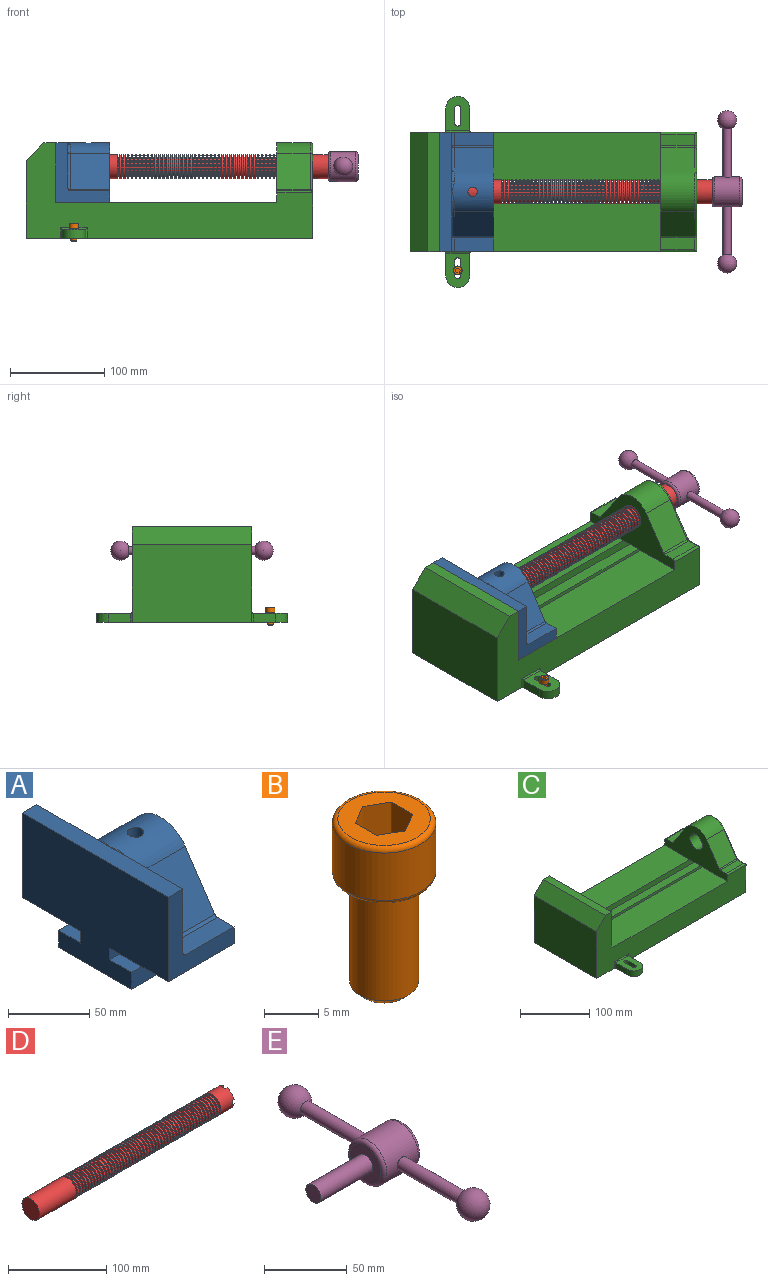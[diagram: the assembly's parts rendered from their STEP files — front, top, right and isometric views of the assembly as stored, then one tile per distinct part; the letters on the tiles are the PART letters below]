
ASSEMBLY  parts=5 mates=5
PART A: 36 faces, bbox 57.2x127x89 mm
  f0: plane 57.15x50.8mm, normal (0,0,-1), area 2903.2mm2, adj f6,f9,f10,f23
  f1: cylinder r=12.7mm len=44.45mm, axis (1,0,0), area 3464.3mm2, adj f6,f15,f16
  f2: plane 41.91x14.52mm, normal (0,0,1), area 608.5mm2, adj f6,f11,f24,f25
  f3: plane 51.86x48.26mm, normal (1,0,0), area 1495.7mm2, adj f8,f10,f31,f33,f35
  f4: plane 51.86x48.26mm, normal (1,0,0), area 1495.7mm2, adj f8,f11,f24,f28,f29
  f5: plane 57.15x50.8mm, normal (0,0,-1), area 2903.2mm2, adj f6,f9,f11,f22
  f6: plane 127x85.09mm, normal (1,0,0), area 5190.6mm2, adj f0,f1,f2,f5,f7,f10,f11,f12
  f7: plane 41.91x14.52mm, normal (0,0,1), area 608.5mm2, adj f6,f10,f30,f31
  f8: plane 127x12.7mm, normal (0,0,1), area 1612.9mm2, adj f3,f4,f9,f10,f11,f26,f34
  f9: plane 127x85.09mm, normal (-1,0,0), area 9096.8mm2, adj f0,f5,f8,f10,f11,f17,f18,f19
  f10: plane 63.5x57.15mm, normal (0,-1,0), area 1372.3mm2, adj f0,f3,f6,f7,f8,f9,f31
  f11: plane 63.5x57.15mm, normal (0,1,0), area 1372.3mm2, adj f2,f4,f5,f6,f8,f9,f24
  f12: plane 41.91x38.43mm, normal (0,-0.83,0.56), area 1939.2mm2, adj f6,f13,f30,f33
  f13: cylinder r=25.4mm len=44.45mm, axis (1,0,0), area 2026.5mm2, adj f6,f12,f14,f16,f26,f28,f34,f35
  f14: plane 41.91x38.43mm, normal (0,0.83,0.56), area 1939.2mm2, adj f6,f13,f25,f29
  f15: plane 25.4x25.4mm, normal (1,0,0), area 506.7mm2, adj f1
  f16: cylinder r=5.08mm len=13.76mm, axis (0,0,1), area 414mm2, adj f1,f13
  f17: plane 57.15x19.05mm, normal (0,0,1), area 1088.7mm2, adj f6,f9,f18,f23
  f18: plane 57.15x12.7mm, normal (0,-1,0), area 725.8mm2, adj f6,f9,f17,f19
  f19: plane 63.5x57.15mm, normal (0,0,-1), area 3629mm2, adj f6,f9,f18,f20
  f20: plane 57.15x12.7mm, normal (0,1,0), area 725.8mm2, adj f6,f9,f19,f21
  f21: plane 57.15x19.05mm, normal (0,0,1), area 1088.7mm2, adj f6,f9,f20,f22
  f22: plane 57.15x8.89mm, normal (0,1,0), area 508.1mm2, adj f5,f6,f9,f21
  f23: plane 57.15x8.89mm, normal (0,-1,0), area 508.1mm2, adj f0,f6,f9,f17
  f24: cylinder r=2.54mm len=14.52mm, axis (0,-1,0), area 57.9mm2, adj f2,f4,f11,f27
  f25: cylinder r=2.54mm len=41.91mm, axis (1,0,0), area 104.3mm2, adj f2,f6,f14,f27
  f26: bspline ~12.24x2.8mm, area 20.9mm2, adj f8,f13,f28
  f27: sphere r=2.54mm, area 6.3mm2, adj f24,f25,f29
  f28: torus R=27.94mm, axis (1,0,0), area 57.8mm2, adj f4,f13,f26,f29
  f29: cylinder r=2.54mm len=39.84mm, axis (0,-0.56,0.83), area 184.6mm2, adj f4,f14,f27,f28
  f30: cylinder r=2.54mm len=41.91mm, axis (1,0,0), area 104.3mm2, adj f6,f7,f12,f32
  f31: cylinder r=2.54mm len=14.52mm, axis (0,-1,0), area 57.9mm2, adj f3,f7,f10,f32
  f32: sphere r=2.54mm, area 6.3mm2, adj f30,f31,f33
  f33: cylinder r=2.54mm len=39.84mm, axis (0,-0.56,-0.83), area 184.6mm2, adj f3,f12,f32,f35
  f34: bspline ~12.24x2.8mm, area 20.9mm2, adj f8,f13,f35
  f35: torus R=27.94mm, axis (1,0,0), area 57.8mm2, adj f3,f13,f33,f34
PART B: 15 faces, bbox 10.3x10.3x19.1 mm
  f0: plane 8.51x8.51mm, normal (0,0,1), area 37.2mm2, adj f5,f6,f7,f8,f9,f10,f14
  f1: cylinder r=3.17mm len=11.94mm, axis (0,0,1), area 238.2mm2, adj f4,f12
  f2: plane 4.83x4.83mm, normal (0,0,-1), area 18.3mm2, adj f12
  f3: cylinder r=4.76mm len=9.53mm, axis (0,0,-1), area 159.6mm2, adj f13,f14
  f4: plane 8.51x8.51mm, normal (0,0,-1), area 25.2mm2, adj f1,f13
  f5: plane 4.83x2.38mm, normal (-0.5,-0.87,0), area 13.3mm2, adj f0,f6,f10,f11
  f6: plane 4.83x2.38mm, normal (0.5,-0.87,0), area 13.3mm2, adj f0,f5,f7,f11
  f7: plane 4.83x2.75mm, normal (1,0,0), area 13.3mm2, adj f0,f6,f8,f11
  f8: plane 4.83x2.38mm, normal (0.5,0.87,0), area 13.3mm2, adj f0,f7,f9,f11
  f9: plane 4.83x2.38mm, normal (-0.5,0.87,0), area 13.3mm2, adj f0,f8,f10,f11
  f10: plane 4.83x2.75mm, normal (-1,0,0), area 13.3mm2, adj f0,f5,f9,f11
  f11: plane 5.5x4.76mm, normal (0,0,1), area 19.6mm2, adj f5,f6,f7,f8,f9,f10
  f12: cone r=3.17mm half-angle=45deg, axis (0,0,1), area 18.9mm2, adj f1,f2
  f13: torus R=4.25mm, axis (0,0,1), area 23mm2, adj f3,f4
  f14: torus R=4.25mm, axis (0,0,1), area 23mm2, adj f0,f3
PART C: 61 faces, bbox 304.8x203.2x103.7 mm
  f0: plane 304.8x101.6mm, normal (0,1,0), area 13520.3mm2, adj f3,f4,f5,f6,f7,f8,f9,f16
  f1: plane 304.8x101.6mm, normal (0,-1,0), area 13520.3mm2, adj f2,f3,f5,f6,f7,f8,f9,f16
  f2: plane 234.95x50.8mm, normal (0,0,1), area 11935.5mm2, adj f1,f5,f16,f26
  f3: plane 127x99.06mm, normal (1,0,0), area 7097.5mm2, adj f0,f1,f9,f14,f17,f18,f19,f20
  f4: plane 234.95x50.8mm, normal (0,0,1), area 11935.5mm2, adj f0,f5,f16,f27
  f5: plane 127x101.6mm, normal (1,0,0), area 9516.1mm2, adj f0,f1,f2,f4,f6,f9,f18,f19
  f6: plane 127x12.7mm, normal (0,0,1), area 1612.9mm2, adj f0,f1,f5,f7
  f7: plane 127x19.05mm, normal (-0.71,0,0.71), area 3421.5mm2, adj f0,f1,f6,f8
  f8: plane 127x82.55mm, normal (-1,0,0), area 10483.8mm2, adj f0,f1,f7,f9
  f9: plane 304.8x203.2mm, normal (0,0,-1), area 33298.3mm2, adj f0,f1,f3,f5,f8,f21,f22,f39
  f10: plane 35.56x11.98mm, normal (0,0,1), area 426mm2, adj f16,f28,f29,f30
  f11: plane 38.43x35.56mm, normal (0,0.83,0.56), area 1645.4mm2, adj f12,f16,f29,f32
  f12: cylinder r=25.4mm len=42.19mm, axis (1,0,0), area 1770.2mm2, adj f11,f13,f16,f33
  f13: plane 38.43x35.56mm, normal (0,-0.83,0.56), area 1645.4mm2, adj f12,f16,f34,f35
  f14: cylinder r=12.7mm len=38.1mm, axis (1,0,0), area 3040.2mm2, adj f3,f16
  f15: plane 35.56x11.98mm, normal (0,0,1), area 426mm2, adj f16,f34,f36,f38
  f16: plane 127x63.5mm, normal (-1,0,0), area 4155.5mm2, adj f0,f1,f2,f4,f10,f11,f12,f13
  f17: plane 38.1x25.4mm, normal (0,0,-1), area 967.7mm2, adj f3,f16,f26,f27
  f18: plane 273.05x19.05mm, normal (0,0,-1), area 5201.6mm2, adj f3,f5,f19,f26
  f19: plane 273.05x12.7mm, normal (0,1,0), area 3467.7mm2, adj f3,f5,f18,f20
  f20: plane 273.05x19.05mm, normal (0,0,1), area 5201.6mm2, adj f3,f5,f19,f21
  f21: plane 273.05x16.51mm, normal (0,1,0), area 4508.1mm2, adj f3,f5,f9,f20
  f22: plane 273.05x16.51mm, normal (0,-1,0), area 4508.1mm2, adj f3,f5,f9,f23
  f23: plane 273.05x19.05mm, normal (0,0,1), area 5201.6mm2, adj f3,f5,f22,f24
  f24: plane 273.05x12.7mm, normal (0,-1,0), area 3467.7mm2, adj f3,f5,f23,f25
  f25: plane 273.05x19.05mm, normal (0,0,-1), area 5201.6mm2, adj f3,f5,f24,f27
  f26: plane 273.05x8.89mm, normal (0,1,0), area 2427.4mm2, adj f2,f3,f5,f17,f18
  f27: plane 273.05x8.89mm, normal (0,-1,0), area 2427.4mm2, adj f3,f4,f5,f17,f25
  f28: cylinder r=2.54mm len=38.1mm, axis (1,0,0), area 148.3mm2, adj f0,f10,f16,f30
  f29: cylinder r=2.54mm len=35.56mm, axis (-1,0,0), area 88.5mm2, adj f10,f11,f16,f31
  f30: cylinder r=2.54mm len=14.52mm, axis (0,1,0), area 54.3mm2, adj f3,f10,f28,f31
  f31: torus R=5.08mm, axis (-1,0,0), area 13.5mm2, adj f3,f29,f30,f32
  f32: cylinder r=2.54mm len=39.84mm, axis (0,0.56,-0.83), area 184.6mm2, adj f3,f11,f31,f33
  f33: torus R=22.86mm, axis (-1,0,0), area 191.4mm2, adj f3,f12,f32,f35
  f34: cylinder r=2.54mm len=35.56mm, axis (-1,0,0), area 88.5mm2, adj f13,f15,f16,f37
  f35: cylinder r=2.54mm len=39.84mm, axis (0,0.56,0.83), area 184.6mm2, adj f3,f13,f33,f37
  f36: cylinder r=2.54mm len=38.1mm, axis (-1,0,0), area 148.3mm2, adj f1,f15,f16,f38
  f37: torus R=5.08mm, axis (-1,0,0), area 13.5mm2, adj f3,f34,f35,f38
  f38: cylinder r=2.54mm len=14.52mm, axis (0,1,0), area 54.3mm2, adj f3,f15,f36,f37
  f39: plane 23.88x9.53mm, normal (-1,0,0), area 227.4mm2, adj f9,f45,f46,f60
  f40: plane 23.88x9.53mm, normal (1,0,0), area 227.4mm2, adj f9,f45,f46,f58
  f41: cylinder r=3.3mm len=9.53mm, axis (0,0,-1), area 98.8mm2, adj f9,f42,f44,f46
  f42: plane 15.62x9.53mm, normal (-1,0,0), area 148.8mm2, adj f9,f41,f43,f46
  f43: cylinder r=3.3mm len=9.53mm, axis (0,0,-1), area 98.8mm2, adj f9,f42,f44,f46
  f44: plane 15.62x9.53mm, normal (1,0,0), area 148.8mm2, adj f9,f41,f43,f46
  f45: cylinder r=12.7mm len=25.4mm, axis (0,0,-1), area 380mm2, adj f9,f39,f40,f46
  f46: plane 36.58x25.4mm, normal (0,0,1), area 722.4mm2, adj f39,f40,f41,f42,f43,f44,f45,f59
  f47: plane 23.88x9.53mm, normal (-1,0,0), area 227.4mm2, adj f9,f53,f54,f56
  f48: plane 23.88x9.53mm, normal (1,0,0), area 227.4mm2, adj f9,f53,f54,f55
  f49: cylinder r=3.3mm len=9.53mm, axis (0,0,-1), area 98.8mm2, adj f9,f50,f52,f54
  f50: plane 15.62x9.53mm, normal (-1,0,0), area 148.8mm2, adj f9,f49,f51,f54
  f51: cylinder r=3.3mm len=9.53mm, axis (0,0,-1), area 98.8mm2, adj f9,f50,f52,f54
  f52: plane 15.62x9.53mm, normal (1,0,0), area 148.8mm2, adj f9,f49,f51,f54
  f53: cylinder r=12.7mm len=25.4mm, axis (0,0,-1), area 380mm2, adj f9,f47,f48,f54
  f54: plane 36.58x25.4mm, normal (0,0,1), area 722.4mm2, adj f47,f48,f49,f50,f51,f52,f53,f57
  f55: cylinder r=1.52mm len=11.05mm, axis (0,0,-1), area 24.1mm2, adj f0,f9,f48,f57
  f56: cylinder r=1.52mm len=11.05mm, axis (0,0,1), area 24.1mm2, adj f0,f9,f47,f57
  f57: cylinder r=1.52mm len=28.45mm, axis (1,0,0), area 63.5mm2, adj f0,f54,f55,f56
  f58: cylinder r=1.52mm len=11.05mm, axis (0,0,1), area 24.1mm2, adj f1,f9,f40,f59
  f59: cylinder r=1.52mm len=28.45mm, axis (-1,0,0), area 63.5mm2, adj f1,f46,f58,f60
  f60: cylinder r=1.52mm len=11.05mm, axis (0,0,-1), area 24.1mm2, adj f1,f9,f39,f59
PART D: 220 faces, bbox 279.4x25.4x25.4 mm
  f0: cylinder r=12.7mm len=25.4mm, axis (-1,0,0), area 1468.2mm2, adj f1,f2,f3,f5,f7,f208,f209,f210
  f1: plane 9.9x9.9mm, normal (1,0,0), area 62.3mm2, adj f0,f4,f213,f216
  f2: plane 9.9x9.9mm, normal (1,0,0), area 62.3mm2, adj f0,f4,f210,f218
  f3: plane 9.9x9.9mm, normal (1,0,0), area 62.3mm2, adj f0,f4,f209,f212
  f4: cylinder r=6.35mm len=25.4mm, axis (1,0,0), area 960.3mm2, adj f1,f2,f3,f5,f6,f208,f209,f210
  f5: plane 9.9x9.9mm, normal (1,0,0), area 62.3mm2, adj f0,f4,f215,f217
  f6: plane 12.7x12.7mm, normal (1,0,0), area 126.7mm2, adj f4
  f7: cone r=12.7mm half-angle=76deg, axis (1,0,0), area 188mm2, adj f0,f9
  f8: cone r=10.16mm half-angle=76deg, axis (-1,0,0), area 188mm2, adj f9,f10
  f9: cylinder r=10.16mm len=20.32mm, axis (1,0,0), area 81.1mm2, adj f7,f8
  f10: cylinder r=12.7mm len=25.4mm, axis (-1,0,0), area 131.7mm2, adj f8,f11
  f11: cone r=12.7mm half-angle=76deg, axis (1,0,0), area 188mm2, adj f10,f13
  f12: cone r=10.16mm half-angle=76deg, axis (-1,0,0), area 188mm2, adj f13,f14
  f13: cylinder r=10.16mm len=20.32mm, axis (1,0,0), area 81.1mm2, adj f11,f12
  f14: cylinder r=12.7mm len=25.4mm, axis (-1,0,0), area 131.7mm2, adj f12,f15
  f15: cone r=12.7mm half-angle=76deg, axis (1,0,0), area 188mm2, adj f14,f17
  f16: cone r=10.16mm half-angle=76deg, axis (-1,0,0), area 188mm2, adj f17,f18
  f17: cylinder r=10.16mm len=20.32mm, axis (1,0,0), area 81.1mm2, adj f15,f16
  f18: cylinder r=12.7mm len=25.4mm, axis (-1,0,0), area 131.7mm2, adj f16,f19
  f19: cone r=12.7mm half-angle=76deg, axis (1,0,0), area 188mm2, adj f18,f21
  f20: cone r=10.16mm half-angle=76deg, axis (-1,0,0), area 188mm2, adj f21,f22
  f21: cylinder r=10.16mm len=20.32mm, axis (1,0,0), area 81.1mm2, adj f19,f20
  f22: cylinder r=12.7mm len=25.4mm, axis (-1,0,0), area 131.7mm2, adj f20,f23
  f23: cone r=12.7mm half-angle=76deg, axis (1,0,0), area 188mm2, adj f22,f25
  f24: cone r=10.16mm half-angle=76deg, axis (-1,0,0), area 188mm2, adj f25,f26
  f25: cylinder r=10.16mm len=20.32mm, axis (1,0,0), area 81.1mm2, adj f23,f24
  f26: cylinder r=12.7mm len=25.4mm, axis (-1,0,0), area 131.7mm2, adj f24,f27
  f27: cone r=12.7mm half-angle=76deg, axis (1,0,0), area 188mm2, adj f26,f29
  f28: cone r=10.16mm half-angle=76deg, axis (-1,0,0), area 188mm2, adj f29,f30
  f29: cylinder r=10.16mm len=20.32mm, axis (1,0,0), area 81.1mm2, adj f27,f28
  f30: cylinder r=12.7mm len=25.4mm, axis (-1,0,0), area 131.7mm2, adj f28,f31
  f31: cone r=12.7mm half-angle=76deg, axis (1,0,0), area 188mm2, adj f30,f33
  f32: cone r=10.16mm half-angle=76deg, axis (-1,0,0), area 188mm2, adj f33,f34
  f33: cylinder r=10.16mm len=20.32mm, axis (1,0,0), area 81.1mm2, adj f31,f32
  f34: cylinder r=12.7mm len=25.4mm, axis (-1,0,0), area 131.7mm2, adj f32,f35
  f35: cone r=12.7mm half-angle=76deg, axis (1,0,0), area 188mm2, adj f34,f37
  f36: cone r=10.16mm half-angle=76deg, axis (-1,0,0), area 188mm2, adj f37,f38
  f37: cylinder r=10.16mm len=20.32mm, axis (1,0,0), area 81.1mm2, adj f35,f36
  f38: cylinder r=12.7mm len=25.4mm, axis (-1,0,0), area 131.7mm2, adj f36,f39
  f39: cone r=12.7mm half-angle=76deg, axis (1,0,0), area 188mm2, adj f38,f41
  f40: cone r=10.16mm half-angle=76deg, axis (-1,0,0), area 188mm2, adj f41,f42
  f41: cylinder r=10.16mm len=20.32mm, axis (1,0,0), area 81.1mm2, adj f39,f40
  f42: cylinder r=12.7mm len=25.4mm, axis (-1,0,0), area 131.7mm2, adj f40,f43
  f43: cone r=12.7mm half-angle=76deg, axis (1,0,0), area 188mm2, adj f42,f45
  f44: cone r=10.16mm half-angle=76deg, axis (-1,0,0), area 188mm2, adj f45,f46
  f45: cylinder r=10.16mm len=20.32mm, axis (1,0,0), area 81.1mm2, adj f43,f44
  f46: cylinder r=12.7mm len=25.4mm, axis (-1,0,0), area 131.7mm2, adj f44,f47
  f47: cone r=12.7mm half-angle=76deg, axis (1,0,0), area 188mm2, adj f46,f49
  f48: cone r=10.16mm half-angle=76deg, axis (-1,0,0), area 188mm2, adj f49,f50
  f49: cylinder r=10.16mm len=20.32mm, axis (1,0,0), area 81.1mm2, adj f47,f48
  f50: cylinder r=12.7mm len=25.4mm, axis (-1,0,0), area 131.7mm2, adj f48,f51
  f51: cone r=12.7mm half-angle=76deg, axis (1,0,0), area 188mm2, adj f50,f53
  f52: cone r=10.16mm half-angle=76deg, axis (-1,0,0), area 188mm2, adj f53,f54
  f53: cylinder r=10.16mm len=20.32mm, axis (1,0,0), area 81.1mm2, adj f51,f52
  f54: cylinder r=12.7mm len=25.4mm, axis (-1,0,0), area 131.7mm2, adj f52,f55
  f55: cone r=12.7mm half-angle=76deg, axis (1,0,0), area 188mm2, adj f54,f57
  f56: cone r=10.16mm half-angle=76deg, axis (-1,0,0), area 188mm2, adj f57,f58
  f57: cylinder r=10.16mm len=20.32mm, axis (1,0,0), area 81.1mm2, adj f55,f56
  f58: cylinder r=12.7mm len=25.4mm, axis (-1,0,0), area 131.7mm2, adj f56,f59
  f59: cone r=12.7mm half-angle=76deg, axis (1,0,0), area 188mm2, adj f58,f61
  f60: cone r=10.16mm half-angle=76deg, axis (-1,0,0), area 188mm2, adj f61,f62
  f61: cylinder r=10.16mm len=20.32mm, axis (1,0,0), area 81.1mm2, adj f59,f60
  f62: cylinder r=12.7mm len=25.4mm, axis (-1,0,0), area 131.7mm2, adj f60,f63
  f63: cone r=12.7mm half-angle=76deg, axis (1,0,0), area 188mm2, adj f62,f65
  f64: cone r=10.16mm half-angle=76deg, axis (-1,0,0), area 188mm2, adj f65,f66
  f65: cylinder r=10.16mm len=20.32mm, axis (1,0,0), area 81.1mm2, adj f63,f64
  f66: cylinder r=12.7mm len=25.4mm, axis (-1,0,0), area 131.7mm2, adj f64,f67
  f67: cone r=12.7mm half-angle=76deg, axis (1,0,0), area 188mm2, adj f66,f69
  f68: cone r=10.16mm half-angle=76deg, axis (-1,0,0), area 188mm2, adj f69,f70
  f69: cylinder r=10.16mm len=20.32mm, axis (1,0,0), area 81.1mm2, adj f67,f68
  f70: cylinder r=12.7mm len=25.4mm, axis (-1,0,0), area 131.7mm2, adj f68,f71
  f71: cone r=12.7mm half-angle=76deg, axis (1,0,0), area 188mm2, adj f70,f73
  f72: cone r=10.16mm half-angle=76deg, axis (-1,0,0), area 188mm2, adj f73,f74
  f73: cylinder r=10.16mm len=20.32mm, axis (1,0,0), area 81.1mm2, adj f71,f72
  f74: cylinder r=12.7mm len=25.4mm, axis (-1,0,0), area 131.7mm2, adj f72,f75
  f75: cone r=12.7mm half-angle=76deg, axis (1,0,0), area 188mm2, adj f74,f77
  f76: cone r=10.16mm half-angle=76deg, axis (-1,0,0), area 188mm2, adj f77,f78
  f77: cylinder r=10.16mm len=20.32mm, axis (1,0,0), area 81.1mm2, adj f75,f76
  f78: cylinder r=12.7mm len=25.4mm, axis (-1,0,0), area 131.7mm2, adj f76,f79
  f79: cone r=12.7mm half-angle=76deg, axis (1,0,0), area 188mm2, adj f78,f81
  f80: cone r=10.16mm half-angle=76deg, axis (-1,0,0), area 188mm2, adj f81,f82
  f81: cylinder r=10.16mm len=20.32mm, axis (1,0,0), area 81.1mm2, adj f79,f80
  f82: cylinder r=12.7mm len=25.4mm, axis (-1,0,0), area 131.7mm2, adj f80,f83
  f83: cone r=12.7mm half-angle=76deg, axis (1,0,0), area 188mm2, adj f82,f85
  f84: cone r=10.16mm half-angle=76deg, axis (-1,0,0), area 188mm2, adj f85,f86
  f85: cylinder r=10.16mm len=20.32mm, axis (1,0,0), area 81.1mm2, adj f83,f84
  f86: cylinder r=12.7mm len=25.4mm, axis (-1,0,0), area 131.7mm2, adj f84,f87
  f87: cone r=12.7mm half-angle=76deg, axis (1,0,0), area 188mm2, adj f86,f89
  f88: cone r=10.16mm half-angle=76deg, axis (-1,0,0), area 188mm2, adj f89,f90
  f89: cylinder r=10.16mm len=20.32mm, axis (1,0,0), area 81.1mm2, adj f87,f88
  f90: cylinder r=12.7mm len=25.4mm, axis (-1,0,0), area 131.7mm2, adj f88,f91
  f91: cone r=12.7mm half-angle=76deg, axis (1,0,0), area 188mm2, adj f90,f93
  f92: cone r=10.16mm half-angle=76deg, axis (-1,0,0), area 188mm2, adj f93,f94
  f93: cylinder r=10.16mm len=20.32mm, axis (1,0,0), area 81.1mm2, adj f91,f92
  f94: cylinder r=12.7mm len=25.4mm, axis (-1,0,0), area 131.7mm2, adj f92,f95
  f95: cone r=12.7mm half-angle=76deg, axis (1,0,0), area 188mm2, adj f94,f97
  f96: cone r=10.16mm half-angle=76deg, axis (-1,0,0), area 188mm2, adj f97,f98
  f97: cylinder r=10.16mm len=20.32mm, axis (1,0,0), area 81.1mm2, adj f95,f96
  f98: cylinder r=12.7mm len=25.4mm, axis (-1,0,0), area 131.7mm2, adj f96,f99
  f99: cone r=12.7mm half-angle=76deg, axis (1,0,0), area 188mm2, adj f98,f101
  f100: cone r=10.16mm half-angle=76deg, axis (-1,0,0), area 188mm2, adj f101,f102
  f101: cylinder r=10.16mm len=20.32mm, axis (1,0,0), area 81.1mm2, adj f99,f100
  f102: cylinder r=12.7mm len=25.4mm, axis (-1,0,0), area 131.7mm2, adj f100,f103
  f103: cone r=12.7mm half-angle=76deg, axis (1,0,0), area 188mm2, adj f102,f105
  f104: cone r=10.16mm half-angle=76deg, axis (-1,0,0), area 188mm2, adj f105,f106
  f105: cylinder r=10.16mm len=20.32mm, axis (1,0,0), area 81.1mm2, adj f103,f104
  f106: cylinder r=12.7mm len=25.4mm, axis (-1,0,0), area 131.7mm2, adj f104,f107
  f107: cone r=12.7mm half-angle=76deg, axis (1,0,0), area 188mm2, adj f106,f109
  f108: cone r=10.16mm half-angle=76deg, axis (-1,0,0), area 188mm2, adj f109,f110
  f109: cylinder r=10.16mm len=20.32mm, axis (1,0,0), area 81.1mm2, adj f107,f108
  f110: cylinder r=12.7mm len=25.4mm, axis (-1,0,0), area 131.7mm2, adj f108,f111
  f111: cone r=12.7mm half-angle=76deg, axis (1,0,0), area 188mm2, adj f110,f113
  f112: cone r=10.16mm half-angle=76deg, axis (-1,0,0), area 188mm2, adj f113,f114
  f113: cylinder r=10.16mm len=20.32mm, axis (1,0,0), area 81.1mm2, adj f111,f112
  f114: cylinder r=12.7mm len=25.4mm, axis (-1,0,0), area 131.7mm2, adj f112,f115
  f115: cone r=12.7mm half-angle=76deg, axis (1,0,0), area 188mm2, adj f114,f117
  f116: cone r=10.16mm half-angle=76deg, axis (-1,0,0), area 188mm2, adj f117,f118
  f117: cylinder r=10.16mm len=20.32mm, axis (1,0,0), area 81.1mm2, adj f115,f116
  f118: cylinder r=12.7mm len=25.4mm, axis (-1,0,0), area 131.7mm2, adj f116,f119
  f119: cone r=12.7mm half-angle=76deg, axis (1,0,0), area 188mm2, adj f118,f121
  f120: cone r=10.16mm half-angle=76deg, axis (-1,0,0), area 188mm2, adj f121,f122
  f121: cylinder r=10.16mm len=20.32mm, axis (1,0,0), area 81.1mm2, adj f119,f120
  f122: cylinder r=12.7mm len=25.4mm, axis (-1,0,0), area 131.7mm2, adj f120,f123
  f123: cone r=12.7mm half-angle=76deg, axis (1,0,0), area 188mm2, adj f122,f125
  f124: cone r=10.16mm half-angle=76deg, axis (-1,0,0), area 188mm2, adj f125,f126
  f125: cylinder r=10.16mm len=20.32mm, axis (1,0,0), area 81.1mm2, adj f123,f124
  f126: cylinder r=12.7mm len=25.4mm, axis (-1,0,0), area 131.7mm2, adj f124,f127
  f127: cone r=12.7mm half-angle=76deg, axis (1,0,0), area 188mm2, adj f126,f129
  f128: cone r=10.16mm half-angle=76deg, axis (-1,0,0), area 188mm2, adj f129,f130
  f129: cylinder r=10.16mm len=20.32mm, axis (1,0,0), area 81.1mm2, adj f127,f128
  f130: cylinder r=12.7mm len=25.4mm, axis (-1,0,0), area 131.7mm2, adj f128,f131
  f131: cone r=12.7mm half-angle=76deg, axis (1,0,0), area 188mm2, adj f130,f133
  f132: cone r=10.16mm half-angle=76deg, axis (-1,0,0), area 188mm2, adj f133,f134
  f133: cylinder r=10.16mm len=20.32mm, axis (1,0,0), area 81.1mm2, adj f131,f132
  f134: cylinder r=12.7mm len=25.4mm, axis (-1,0,0), area 131.7mm2, adj f132,f135
  f135: cone r=12.7mm half-angle=76deg, axis (1,0,0), area 188mm2, adj f134,f137
  f136: cone r=10.16mm half-angle=76deg, axis (-1,0,0), area 188mm2, adj f137,f138
  f137: cylinder r=10.16mm len=20.32mm, axis (1,0,0), area 81.1mm2, adj f135,f136
  f138: cylinder r=12.7mm len=25.4mm, axis (-1,0,0), area 131.7mm2, adj f136,f139
  f139: cone r=12.7mm half-angle=76deg, axis (1,0,0), area 188mm2, adj f138,f141
  f140: cone r=10.16mm half-angle=76deg, axis (-1,0,0), area 188mm2, adj f141,f142
  f141: cylinder r=10.16mm len=20.32mm, axis (1,0,0), area 81.1mm2, adj f139,f140
  f142: cylinder r=12.7mm len=25.4mm, axis (-1,0,0), area 131.7mm2, adj f140,f143
  f143: cone r=12.7mm half-angle=76deg, axis (1,0,0), area 188mm2, adj f142,f145
  f144: cone r=10.16mm half-angle=76deg, axis (-1,0,0), area 188mm2, adj f145,f146
  f145: cylinder r=10.16mm len=20.32mm, axis (1,0,0), area 81.1mm2, adj f143,f144
  f146: cylinder r=12.7mm len=25.4mm, axis (-1,0,0), area 131.7mm2, adj f144,f147
  f147: cone r=12.7mm half-angle=76deg, axis (1,0,0), area 188mm2, adj f146,f149
  f148: cone r=10.16mm half-angle=76deg, axis (-1,0,0), area 188mm2, adj f149,f150
  f149: cylinder r=10.16mm len=20.32mm, axis (1,0,0), area 81.1mm2, adj f147,f148
  f150: cylinder r=12.7mm len=25.4mm, axis (-1,0,0), area 131.7mm2, adj f148,f151
  f151: cone r=12.7mm half-angle=76deg, axis (1,0,0), area 188mm2, adj f150,f153
  f152: cone r=10.16mm half-angle=76deg, axis (-1,0,0), area 188mm2, adj f153,f154
  f153: cylinder r=10.16mm len=20.32mm, axis (1,0,0), area 81.1mm2, adj f151,f152
  f154: cylinder r=12.7mm len=25.4mm, axis (-1,0,0), area 131.7mm2, adj f152,f155
  f155: cone r=12.7mm half-angle=76deg, axis (1,0,0), area 188mm2, adj f154,f157
  f156: cone r=10.16mm half-angle=76deg, axis (-1,0,0), area 188mm2, adj f157,f158
  f157: cylinder r=10.16mm len=20.32mm, axis (1,0,0), area 81.1mm2, adj f155,f156
  f158: cylinder r=12.7mm len=25.4mm, axis (-1,0,0), area 131.7mm2, adj f156,f159
  f159: cone r=12.7mm half-angle=76deg, axis (1,0,0), area 188mm2, adj f158,f161
  f160: cone r=10.16mm half-angle=76deg, axis (-1,0,0), area 188mm2, adj f161,f162
  f161: cylinder r=10.16mm len=20.32mm, axis (1,0,0), area 81.1mm2, adj f159,f160
  f162: cylinder r=12.7mm len=25.4mm, axis (-1,0,0), area 131.7mm2, adj f160,f163
  f163: cone r=12.7mm half-angle=76deg, axis (1,0,0), area 188mm2, adj f162,f165
  f164: cone r=10.16mm half-angle=76deg, axis (-1,0,0), area 188mm2, adj f165,f166
  f165: cylinder r=10.16mm len=20.32mm, axis (1,0,0), area 81.1mm2, adj f163,f164
  f166: cylinder r=12.7mm len=25.4mm, axis (-1,0,0), area 131.7mm2, adj f164,f167
  f167: cone r=12.7mm half-angle=76deg, axis (1,0,0), area 188mm2, adj f166,f169
  f168: cone r=10.16mm half-angle=76deg, axis (-1,0,0), area 188mm2, adj f169,f170
  f169: cylinder r=10.16mm len=20.32mm, axis (1,0,0), area 81.1mm2, adj f167,f168
  f170: cylinder r=12.7mm len=25.4mm, axis (-1,0,0), area 131.7mm2, adj f168,f171
  f171: cone r=12.7mm half-angle=76deg, axis (1,0,0), area 188mm2, adj f170,f173
  f172: cone r=10.16mm half-angle=76deg, axis (-1,0,0), area 188mm2, adj f173,f174
  f173: cylinder r=10.16mm len=20.32mm, axis (1,0,0), area 81.1mm2, adj f171,f172
  f174: cylinder r=12.7mm len=25.4mm, axis (-1,0,0), area 131.7mm2, adj f172,f175
  f175: cone r=12.7mm half-angle=76deg, axis (1,0,0), area 188mm2, adj f174,f177
  f176: cone r=10.16mm half-angle=76deg, axis (-1,0,0), area 188mm2, adj f177,f178
  f177: cylinder r=10.16mm len=20.32mm, axis (1,0,0), area 81.1mm2, adj f175,f176
  f178: cylinder r=12.7mm len=25.4mm, axis (-1,0,0), area 131.7mm2, adj f176,f179
  f179: cone r=12.7mm half-angle=76deg, axis (1,0,0), area 188mm2, adj f178,f181
  f180: cone r=10.16mm half-angle=76deg, axis (-1,0,0), area 188mm2, adj f181,f182
  f181: cylinder r=10.16mm len=20.32mm, axis (1,0,0), area 81.1mm2, adj f179,f180
  f182: cylinder r=12.7mm len=25.4mm, axis (-1,0,0), area 131.7mm2, adj f180,f183
  f183: cone r=12.7mm half-angle=76deg, axis (1,0,0), area 188mm2, adj f182,f185
  f184: cone r=10.16mm half-angle=76deg, axis (-1,0,0), area 188mm2, adj f185,f186
  f185: cylinder r=10.16mm len=20.32mm, axis (1,0,0), area 81.1mm2, adj f183,f184
  f186: cylinder r=12.7mm len=25.4mm, axis (-1,0,0), area 131.7mm2, adj f184,f187
  f187: cone r=12.7mm half-angle=76deg, axis (1,0,0), area 188mm2, adj f186,f189
  f188: cone r=10.16mm half-angle=76deg, axis (-1,0,0), area 188mm2, adj f189,f190
  f189: cylinder r=10.16mm len=20.32mm, axis (1,0,0), area 81.1mm2, adj f187,f188
  f190: cylinder r=12.7mm len=25.4mm, axis (-1,0,0), area 131.7mm2, adj f188,f191
  f191: cone r=12.7mm half-angle=76deg, axis (1,0,0), area 188mm2, adj f190,f193
  f192: cone r=10.16mm half-angle=76deg, axis (-1,0,0), area 188mm2, adj f193,f194
  f193: cylinder r=10.16mm len=20.32mm, axis (1,0,0), area 81.1mm2, adj f191,f192
  f194: cylinder r=12.7mm len=25.4mm, axis (-1,0,0), area 131.7mm2, adj f192,f195
  f195: cone r=12.7mm half-angle=76deg, axis (1,0,0), area 188mm2, adj f194,f197
  f196: cone r=10.16mm half-angle=76deg, axis (-1,0,0), area 188mm2, adj f197,f198
  f197: cylinder r=10.16mm len=20.32mm, axis (1,0,0), area 81.1mm2, adj f195,f196
  f198: cylinder r=12.7mm len=25.4mm, axis (-1,0,0), area 131.7mm2, adj f196,f199
  f199: cone r=12.7mm half-angle=76deg, axis (1,0,0), area 188mm2, adj f198,f201
  f200: cone r=10.16mm half-angle=76deg, axis (-1,0,0), area 188mm2, adj f201,f202
  f201: cylinder r=10.16mm len=20.32mm, axis (1,0,0), area 81.1mm2, adj f199,f200
  f202: cylinder r=12.7mm len=25.4mm, axis (-1,0,0), area 131.7mm2, adj f200,f203
  f203: cone r=12.7mm half-angle=76deg, axis (1,0,0), area 188mm2, adj f202,f205
  f204: cone r=10.16mm half-angle=76deg, axis (-1,0,0), area 188mm2, adj f205,f207
  f205: cylinder r=10.16mm len=20.32mm, axis (1,0,0), area 81.1mm2, adj f203,f204
  f206: plane 25.4x25.4mm, normal (-1,0,0), area 506.7mm2, adj f207
  f207: cylinder r=12.7mm len=52.45mm, axis (-1,0,0), area 4185.4mm2, adj f204,f206
  f208: plane 6.88x5.08mm, normal (1,0,0), area 32.7mm2, adj f0,f4,f209,f210
  f209: plane 6.62x2.54mm, normal (0,-1,0), area 16.8mm2, adj f0,f3,f4,f208
  f210: plane 6.62x2.54mm, normal (0,1,0), area 16.8mm2, adj f0,f2,f4,f208
  f211: plane 6.88x5.08mm, normal (1,0,0), area 32.7mm2, adj f0,f4,f212,f213
  f212: plane 6.62x2.54mm, normal (0,0,1), area 16.8mm2, adj f0,f3,f4,f211
  f213: plane 6.62x2.54mm, normal (0,0,-1), area 16.8mm2, adj f0,f1,f4,f211
  f214: plane 6.88x5.08mm, normal (1,0,0), area 32.7mm2, adj f0,f4,f215,f216
  f215: plane 6.62x2.54mm, normal (0,1,0), area 16.8mm2, adj f0,f4,f5,f214
  f216: plane 6.62x2.54mm, normal (0,-1,0), area 16.8mm2, adj f0,f1,f4,f214
  f217: plane 6.62x2.54mm, normal (0,0,-1), area 16.8mm2, adj f0,f4,f5,f219
  f218: plane 6.62x2.54mm, normal (0,0,1), area 16.8mm2, adj f0,f2,f4,f219
  f219: plane 6.88x5.08mm, normal (1,0,0), area 32.7mm2, adj f0,f4,f217,f218
PART E: 11 faces, bbox 76.2x172.7x34.4 mm
  f0: sphere r=10.16mm, area 1231.8mm2, adj f1
  f1: cylinder r=4.45mm len=51.82mm, axis (0,1,0), area 1438.5mm2, adj f0,f4
  f2: sphere r=10.16mm, area 1231.8mm2, adj f3
  f3: cylinder r=4.45mm len=51.82mm, axis (0,1,0), area 1438.5mm2, adj f2,f4
  f4: cylinder r=15.88mm len=31.75mm, axis (-1,0,0), area 2534.7mm2, adj f1,f3,f9,f10
  f5: cylinder r=6.35mm len=44.45mm, axis (-1,0,0), area 1773.5mm2, adj f6,f8
  f6: plane 12.7x12.7mm, normal (-1,0,0), area 126.7mm2, adj f5
  f7: plane 26.67x26.67mm, normal (1,0,0), area 558.6mm2, adj f10
  f8: plane 26.67x26.67mm, normal (-1,0,0), area 432mm2, adj f5,f9
  f9: torus R=13.33mm, axis (1,0,0), area 374.8mm2, adj f4,f8
  f10: torus R=13.33mm, axis (1,0,0), area 374.8mm2, adj f4,f7
PLACE A at identity
PLACE B rot(axis=(0,0,1),153.6deg) t=(-254,-83.45,9.52)mm
PLACE C at identity fixed
PLACE D rot(axis=(1,0,0),180deg) t=(0,0,152.4)mm
PLACE E rot(axis=(1,0,0),180deg) t=(-21.59,0,152.4)mm
MATE fastened D.f4 <-> E.f5  axis (1,0,0) through (16.51,0,76.2)mm
MATE planar A.f0 <-> C.f2  axis (0,0,-1) through (-244.48,-38.1,38.1)mm
MATE pin_slot B.f1 <-> C.f41  axis (0,0,1) through (-254,-83.45,9.52)mm
MATE revolute D.f7 <-> A.f28  axis (-1,0,0) through (-260.35,0,76.2)mm
MATE cylindrical C.f12 <-> D.f7  axis (-1,0,0) through (-38.1,0,76.2)mm
